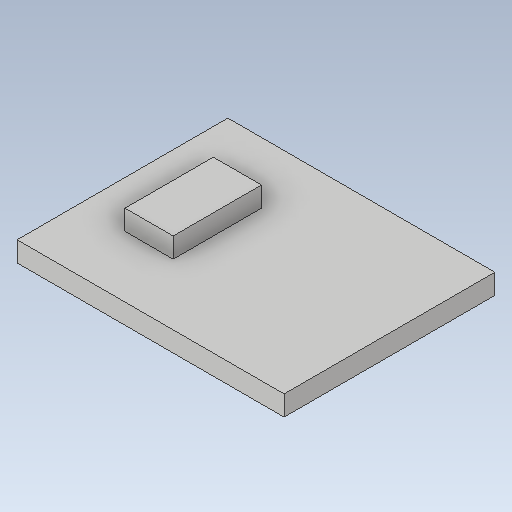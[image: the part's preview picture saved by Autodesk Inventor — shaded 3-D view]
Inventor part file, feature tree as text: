
AUTODESK INVENTOR PART (.ipt)
format: ipt  version: 2020 (Build 240168000, 168)  size: 104,448 bytes
history: native  units: mm
features: extrude x2, sketch x2, other x1
ambient origin geometry x8: Origin, YZ Plane, XZ Plane, XY Plane, X Axis, Y Axis, Z Axis, Center Point
bodies: Body1 (feature_tree)
feature tree (5):
  other  "Bryła1"
  extrude  "Wyciągnięcie proste1"  Depth=10.5mm
  extrude  "Wyciągnięcie proste2"  Depth=5.25mm
  sketch  "Szkic1"
  sketch  "Szkic2"
